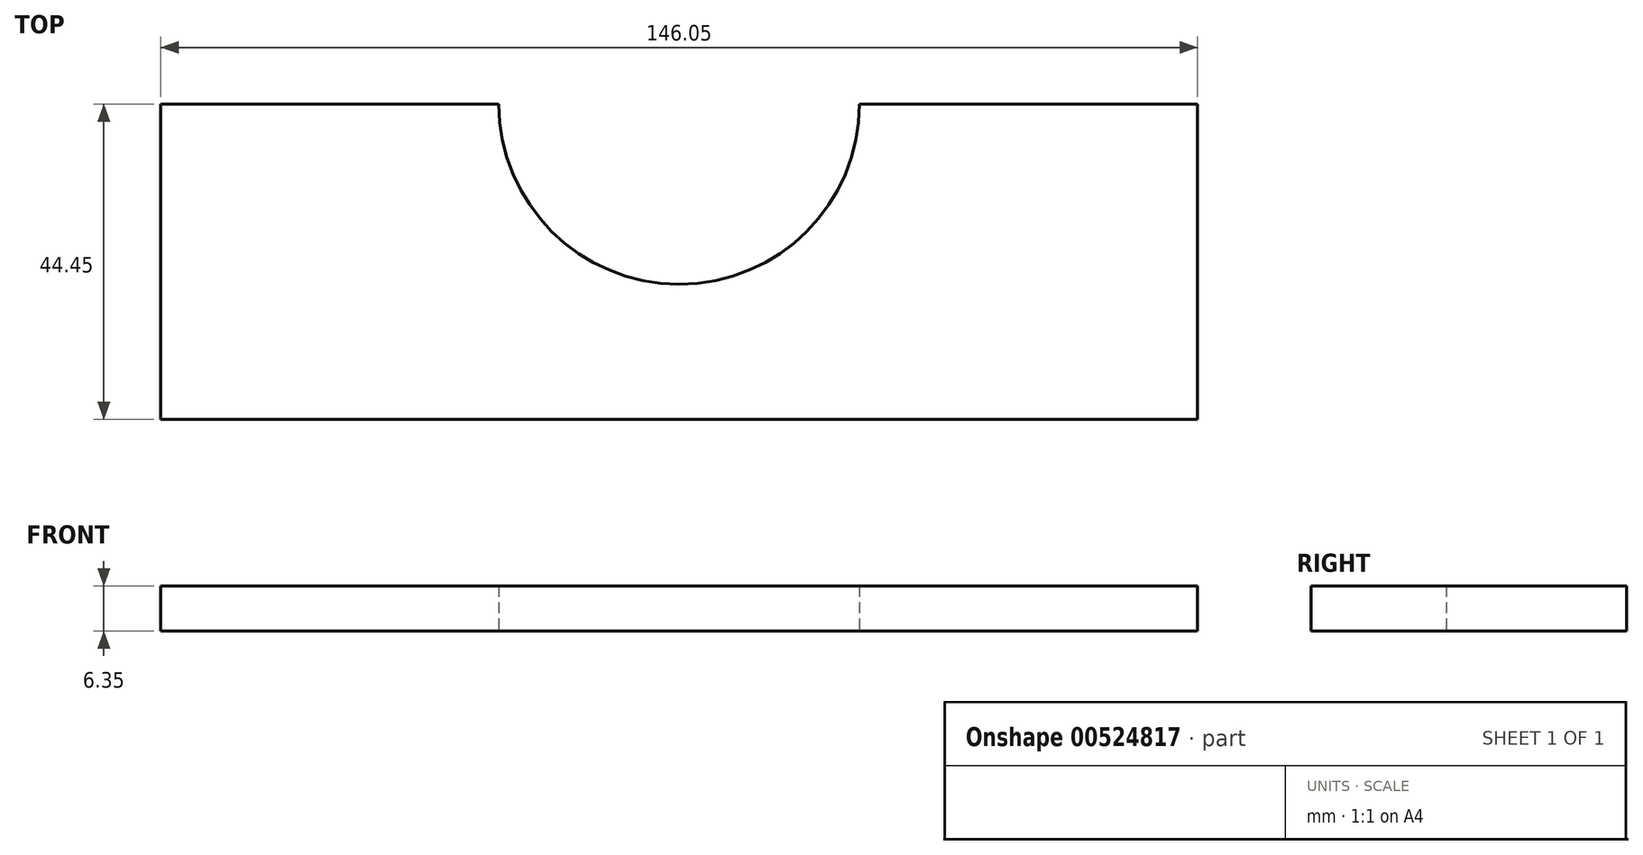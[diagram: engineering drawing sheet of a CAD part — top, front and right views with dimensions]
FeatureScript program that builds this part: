
annotation { "Feature Type Name" : "Feature", "Feature Type Description" : "" }
export const myFeature = defineFeature(function(context is Context, id is Id, definition is map)
    precondition{}
    {
        {
            var Q0;
            Q0=qCreatedBy(makeId("Top.planeOp"),FACE);
            var sketch = newSketch(context, id + "F0", { "sketchPlane" : qUnion([Q0])});
            skLineSegment(sketch, "E0.bottom", {"start": v(0, 0) * mm, "end": v(47.63, 0) * mm});
            skLineSegment(sketch, "E0.top", {"start": v(0, -44.45) * mm, "end": v(146.05, -44.45) * mm});
            skLineSegment(sketch, "E0.left", {"start": v(0, 0) * mm, "end": v(0, -44.45) * mm});
            skLineSegment(sketch, "E0.right", {"start": v(146.05, 0) * mm, "end": v(146.05, -44.45) * mm});
            skArc(sketch, "E1", {"start": v(47.62, 0) * mm, "mid": v(73.03, -25.4) * mm, "end": v(98.43, 0) * mm});
            skLineSegment(sketch, "E2.trimOffspring", {"start": v(98.43, 0) * mm, "end": v(146.05, 0) * mm});
            skSolve(sketch);
        }
        {
            var Q0;
            Q0=makeQuery(id+"F0.imprint","IMPRINT",FACE,{"disambiguationData":[TD([[makeQuery(id+"F0.imprint","IMPRINT",EDGE,{"derivedFrom":sQuery(id+"F0.wireOp",EDGE,"E0.bottom")}),-1.0]])]});
            extrude(context, id + "F1", {"entities" : qUnion([Q0]), "depth" : 6.35 * mm, "offsetDistance" : 25.4 * mm});
        }
    });
